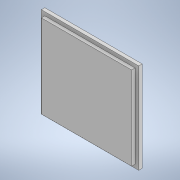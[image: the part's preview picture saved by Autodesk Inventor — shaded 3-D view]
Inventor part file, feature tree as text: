
AUTODESK INVENTOR PART (.ipt)
format: ipt  version: 2022 (Build 260153070, 153G)  size: 105,472 bytes
history: native  units: mm
features: extrude x2, sketch x2
ambient origin geometry x8: Origin, YZ Plane, XZ Plane, XY Plane, X Axis, Y Axis, Z Axis, Center Point
bodies: Body1 (feature_tree)
feature tree (4):
  extrude  "拉伸3"  Depth=130.0mm
  extrude  "拉伸4"  Depth=129.8mm
  sketch  "草图5"  dims[d10=140.0mm d11=130.0mm]
  sketch  "草图6"  dims[d12=5.0mm d13=0.0mm d14=129.8mm d15=119.8mm d22=5.1mm d23=5.1mm d24=5.0mm d25=0.0mm]
